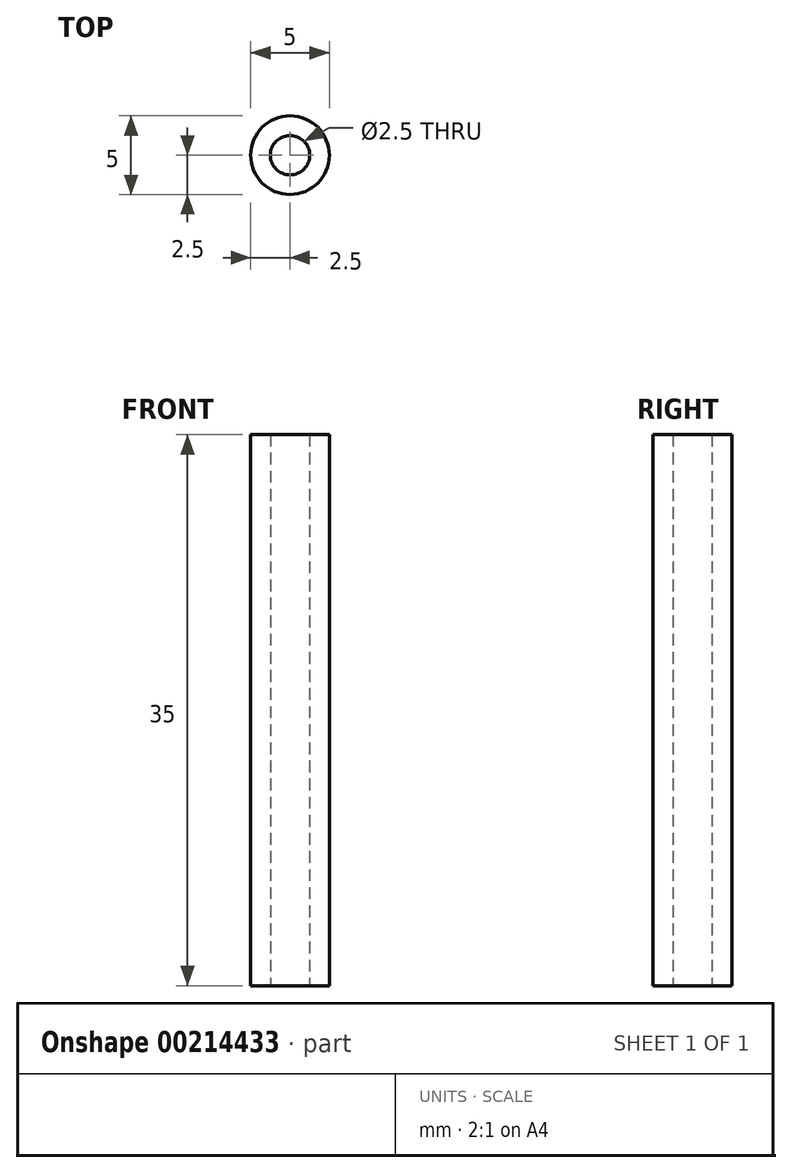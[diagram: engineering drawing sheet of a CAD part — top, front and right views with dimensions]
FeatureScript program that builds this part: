
annotation { "Feature Type Name" : "Feature", "Feature Type Description" : "" }
export const myFeature = defineFeature(function(context is Context, id is Id, definition is map)
    precondition{}
    {
        {
            var Q0;
            Q0=qCreatedBy(makeId("Top.planeOp"),FACE);
            var sketch = newSketch(context, id + "F0", { "sketchPlane" : qUnion([Q0])});
            skCircle(sketch, "E0", {"center": v(0, 0) * mm, "radius": 1.25 * mm});
            skCircle(sketch, "E1", {"center": v(0, 0) * mm, "radius": 2.5 * mm});
            skSolve(sketch);
        }
        {
            var Q0;
            Q0 = qSketchRegion(id + "F0", true);
            extrude(context, id + "F1", {"entities" : qUnion([Q0]), "depth" : 35 * mm});
        }
    });
